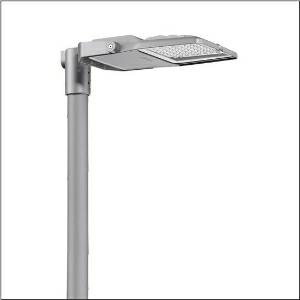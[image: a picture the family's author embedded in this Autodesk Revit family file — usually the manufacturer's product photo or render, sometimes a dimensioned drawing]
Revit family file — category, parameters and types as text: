
# Revit family: floodlight_fl_21_iq_mini___pl43_5xa7772c4a3a_a38e
name_source: partatom
category: Lighting Fixtures
units: mm (PartAtom-declared; Revit-internal decimal feet)

## family parameters
Cut with Voids When Loaded = No
Host = Face
Light Source = No
Part Type = Normal
Room Calculation Point = No
Round Connector Dimension = Use Diameter
Shared = No

## types (1)
- --- (1 x LED, 13050 lm, 87.2 W, 4000K)
    Apparent Load = 87 VA
    CIE Flux Codes = 27 78 99 100 100
    Color Rendering = 70
    Color Temperature = 4000K
    Default Elevation = 1800 mm
    Description = Floodlight FL 21 iQ mini, floodlight, primary light control with lens, of PMMA, primary optical cover: protective disc, of toughened safety glass, transparent, light distribution: PL43, light emission: direct distribution, installation type: surface-mounted, LED, High Power LED, rated luminous flux: 13.050lm, luminous efficacy: 150lm/W, light colour: 740, colour temperature: 4000K, control gear: iQ Street-Remote/DALI, control: Auto-Match, Temp-Guard, Night-Set, Smart-Wire, Desk-Remote (wireless, voltage-free reading and setting of iQ features in the workshop via application-optimized NFC function/RFID function), optimised constant luminous flux control (CLO 2.0), Light-Fading, Lumen-Switch, with terminal, 6-pole, mains connection: 220..240V, AC, 50/60Hz, start of lifetime: 87W, end of service life: 92W, reduction: 40W, luminaire housing, of diecast aluminium, powder-coated, Siteco® metallic grey (DB 702S), corrosivity category C5 mid according to DIN EN ISO 12944, suitable for swimming pools, chlorine-resistant, sealing non-destructively replaceable, please order mast flange separately, mast bracket, of steel, galvanised, powder-coated, protection rating (complete): IP66, insulation class (complete): insulation class II (safety insulation), certification: CE, ENEC, VDE, protection symbol: D, impact resistance: IK08, permissible operating ambient temperature: -40..+40°C, permissible operating ambient temperature for outdoor applications: -40..+50°C, standard: DIN EN 12944, LABS conformity tested according to VDMA 24364:2018-05, packaging unit: 1 piece

Light Distribution: PL43
    Height = 70 mm
    Lamp = 1 x LED
    Lamp Light Flux = 13050 lm
    Lamp Power = 87.2 W
    Lamp count = 1
    Length = 485 mm
    Luminous efficacy = 150 lm/W
    Manufacturer = Siteco
    ModVariant = No
    Model = 5XA7772C4A3A
    Number of Poles = 1
    OnlyDefault = Yes
    Power Factor = 1
    Product Name = Floodlight FL 21 iQ mini | PL43
    Product group = floodlight | pylon annexe
    ProductGroupID = 6201
    Protection Class = Protection class II
    Protection Degree = IP 66
    RLX_Detail_Level = 1
    RLX_Emergency_Light_Flux = 0 lm
    RLX_Emergency_Type = 0
    RLX_Emergency_Type_DB = No
    RlxData = <blob elided: 101349 chars, md5=455f82a9>
    Socket = socket
    Standby Power = 0 W
    System Light Flux = 13050 lm
    System Power = 87 W
    Type Comments = factory setting: luminous flux: 100 % | dim-lin: 254 | 456 mA
    Type Image = l_1007125.jpg
    URL = http://relux.com
    VarID = @adj_183611
    Voltage = 0 V
    Weight = 0.00 kg
    Width = 337 mm

## geometry (parser evidence)
native form markers: Blend x4, Sweep x13
no freeform markers — native parametric forms only
